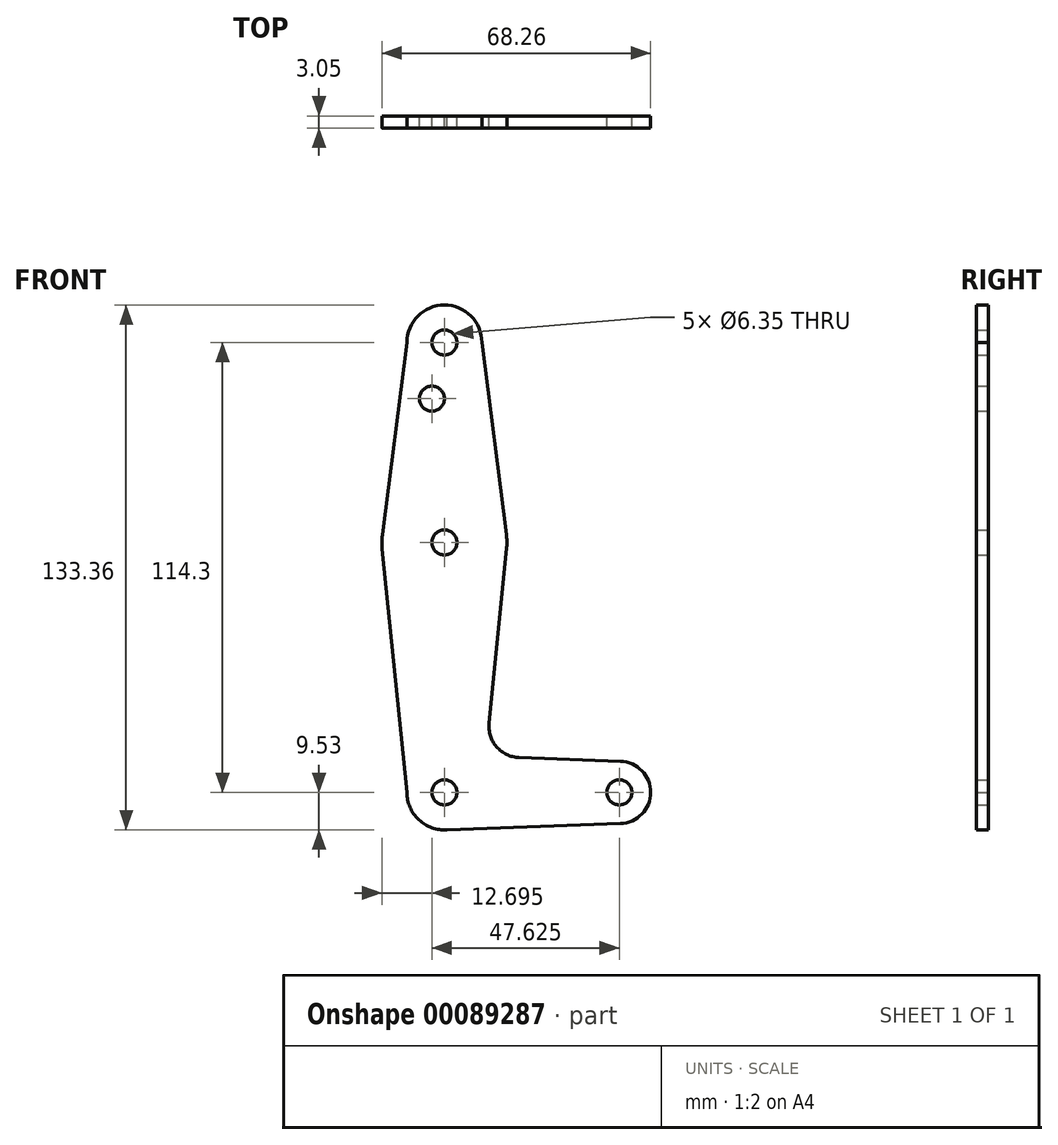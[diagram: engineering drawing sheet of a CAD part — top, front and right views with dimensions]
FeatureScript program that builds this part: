
annotation { "Feature Type Name" : "Feature", "Feature Type Description" : "" }
export const myFeature = defineFeature(function(context is Context, id is Id, definition is map)
    precondition{}
    {
        {
            var Q0;
            Q0=qCreatedBy(makeId("Front.planeOp"),FACE);
            var sketch = newSketch(context, id + "F0", { "sketchPlane" : qUnion([Q0])});
            skLineSegment(sketch, "E0", {"start": v(0, 0) * mm, "end": v(0, 114.3) * mm, "construction": true});
            skLineSegment(sketch, "E1", {"start": v(0, 0) * mm, "end": v(44.45, 0) * mm, "construction": true});
            skCircle(sketch, "E2", {"center": v(0, 0) * mm, "radius": 9.53 * mm});
            skCircle(sketch, "E3", {"center": v(44.45, 0) * mm, "radius": 7.94 * mm});
            skCircle(sketch, "E4", {"center": v(0, 114.3) * mm, "radius": 9.53 * mm});
            skCircle(sketch, "E5", {"center": v(0, 63.5) * mm, "radius": 15.88 * mm});
            skLineSegment(sketch, "E6", {"start": v(18.97, 8.85) * mm, "end": v(44.73, 7.93) * mm});
            skLineSegment(sketch, "E7", {"start": v(0, -9.53) * mm, "end": v(44.73, -7.93) * mm});
            skLineSegment(sketch, "E8", {"start": v(0, 0) * mm, "end": v(-9.53, 0) * mm});
            skLineSegment(sketch, "E9", {"start": v(-9.52, 114.3) * mm, "end": v(-15.75, 65.5) * mm});
            skLineSegment(sketch, "E10", {"start": v(9.52, 114.3) * mm, "end": v(15.75, 65.5) * mm});
            skCircle(sketch, "E11", {"center": v(0, 114.3) * mm, "radius": 3.18 * mm});
            skCircle(sketch, "E12", {"center": v(0, 63.5) * mm, "radius": 3.18 * mm});
            skCircle(sketch, "E13", {"center": v(0, 0) * mm, "radius": 3.18 * mm});
            skCircle(sketch, "E14", {"center": v(44.45, 0) * mm, "radius": 3.18 * mm});
            skCircle(sketch, "E15", {"center": v(-3.18, 100.03) * mm, "radius": 3.18 * mm});
            skLineSegment(sketch, "E16", {"start": v(11.34, 17.6) * mm, "end": v(15.8, 61.91) * mm});
            skLineSegment(sketch, "E17", {"start": v(-9.53, 0) * mm, "end": v(-15.8, 61.9) * mm});
            skArc(sketch, "E18.filletArc", {"start": v(11.34, 17.6) * mm, "mid": v(13.26, 11.57) * mm, "end": v(18.97, 8.85) * mm});
            skSolve(sketch);
        }
        {
            var Q0;
            Q0 = qSketchRegion(id + "F0", true);
            extrude(context, id + "F1", {"entities" : qUnion([Q0]), "depth" : 3.05 * mm});
        }
    });
